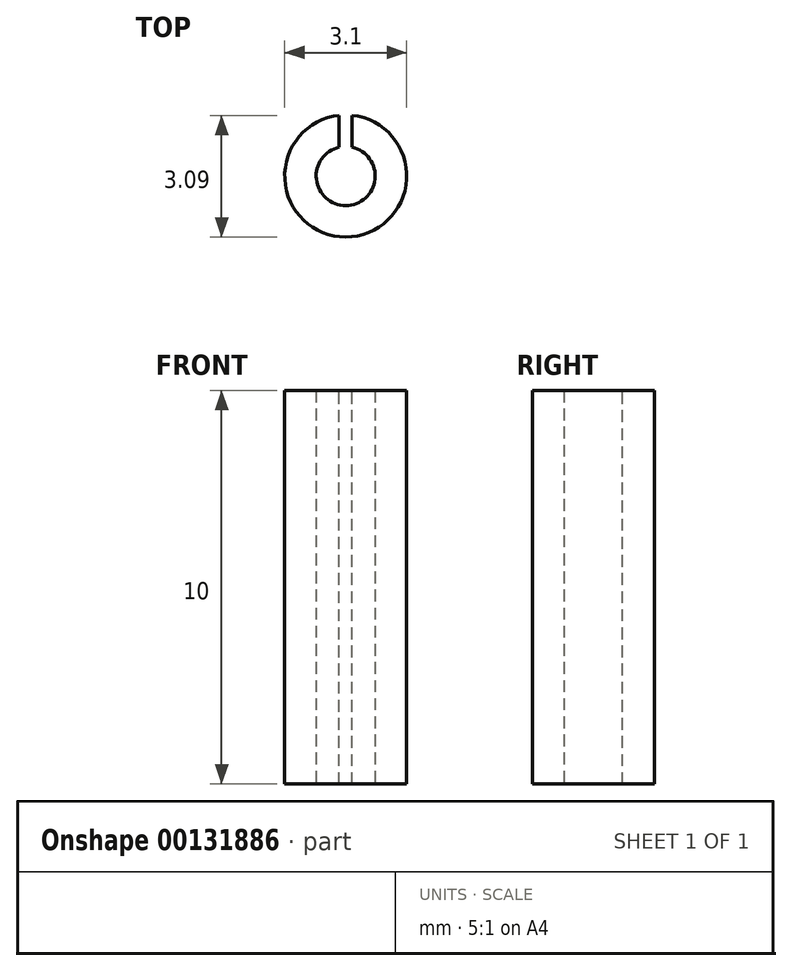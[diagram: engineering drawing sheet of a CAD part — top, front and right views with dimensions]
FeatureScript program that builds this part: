
annotation { "Feature Type Name" : "Feature", "Feature Type Description" : "" }
export const myFeature = defineFeature(function(context is Context, id is Id, definition is map)
    precondition{}
    {
        {
            var Q0;
            Q0=qCreatedBy(makeId("Top.planeOp"),FACE);
            var sketch = newSketch(context, id + "F0", { "sketchPlane" : qUnion([Q0])});
            skCircle(sketch, "E0", {"center": v(0, 0) * mm, "radius": 0.75 * mm});
            skCircle(sketch, "E1", {"center": v(0, 0) * mm, "radius": 1.55 * mm});
            skSolve(sketch);
        }
        {
            var Q0;
            Q0 = qSketchRegion(id + "F0", true);
            extrude(context, id + "F1", {"entities" : qUnion([Q0]), "depth" : 10 * mm});
        }
        {
            var Q0;
            Q0=makeQuery(id+"F1.opExtrude","CAP_FACE",FACE,{"disambiguationData":[OSD([sQuery(id+"F0.wireOp",EDGE,"E0"),sQuery(id+"F0.wireOp",EDGE,"E1")])],"isStart":false});
            var sketch = newSketch(context, id + "F2", { "sketchPlane" : qUnion([Q0])});
            skLineSegment(sketch, "E2.bottom", {"start": v(0.16, 1.66) * mm, "end": v(-0.16, 1.66) * mm});
            skLineSegment(sketch, "E2.top", {"start": v(0.16, 0.62) * mm, "end": v(-0.16, 0.62) * mm});
            skLineSegment(sketch, "E2.left", {"start": v(0.16, 1.66) * mm, "end": v(0.16, 0.62) * mm});
            skLineSegment(sketch, "E2.right", {"start": v(-0.16, 1.66) * mm, "end": v(-0.16, 0.62) * mm});
            skPoint(sketch, "E2.middle", {"position": v(0, 1.14) * mm});
            skSolve(sketch);
        }
        {
            var Q0;
            {var subQ0=sQuery(id+"F2.wireOp",EDGE,"E2.left");var subQ1=makeQuery(id+"F1.opExtrude","CAP_EDGE",EDGE,{"disambiguationData":[OSD([sQuery(id+"F0.wireOp",EDGE,"E1")])],"isStart":false});var subQ2=makeQuery(id+"F2.imprint","INTERSECT",VERTEX,{"derivedFrom":[subQ1,subQ0]});Q0=makeQuery(id+"F2.imprint","IMPRINT",FACE,{"disambiguationData":[TD([[makeQuery(id+"F2.imprint","IMPRINT",EDGE,{"disambiguationData":[TD([[subQ2,-1.0]])],"derivedFrom":subQ0}),-1.0]])]});}
            extrude(context, id + "F3", {"entities" : qUnion([Q0]), "operationType" : NewBodyOperationType.REMOVE, "oppositeDirection" : true, "depth" : 10 * mm});
        }
    });
